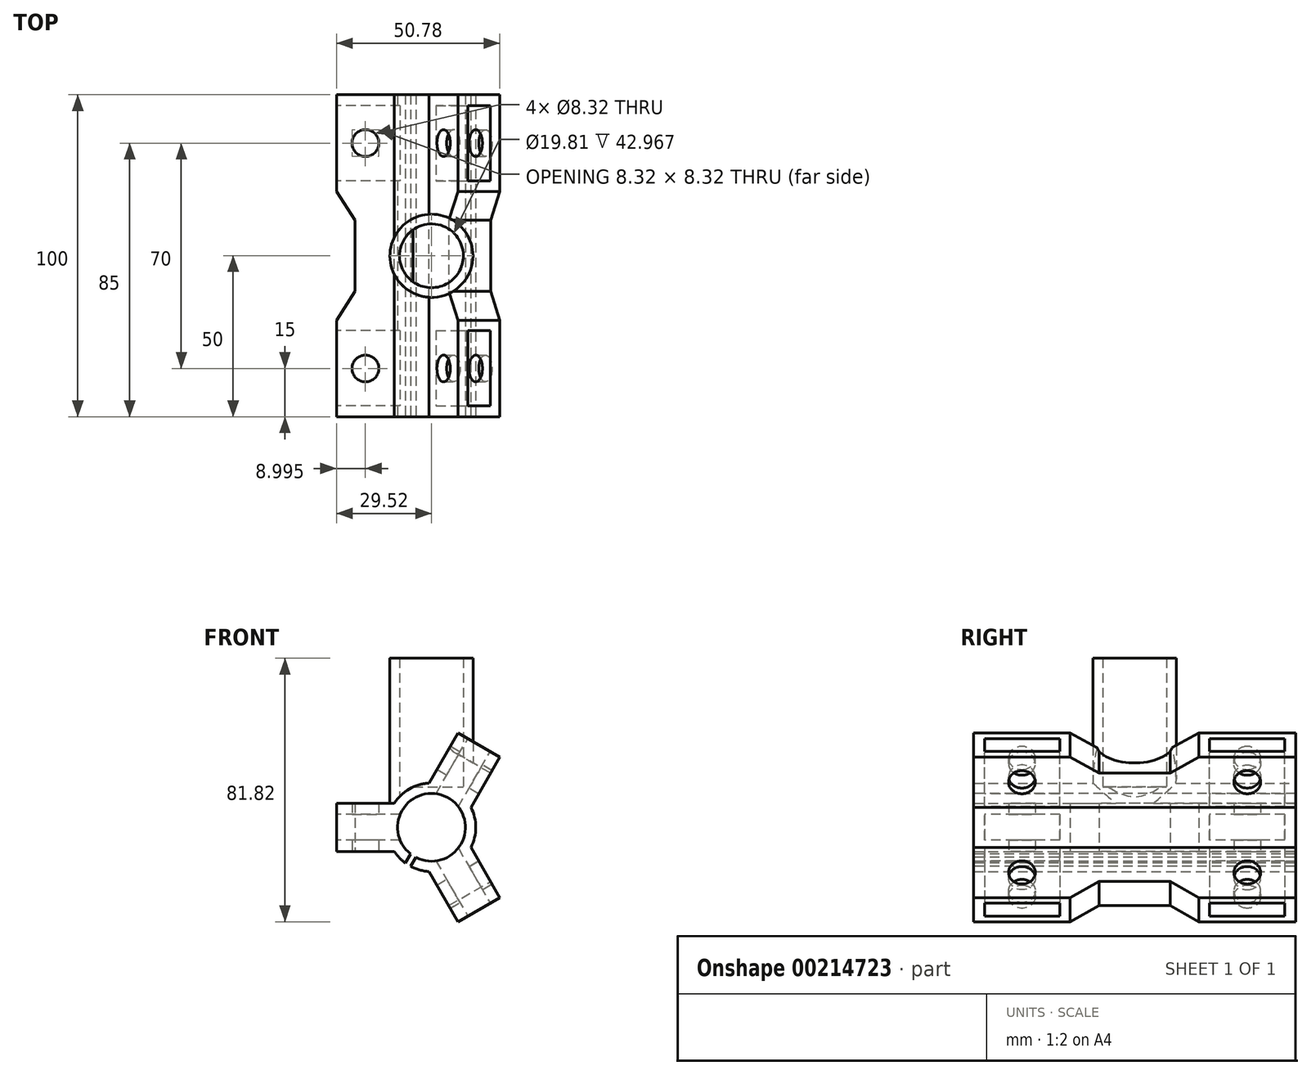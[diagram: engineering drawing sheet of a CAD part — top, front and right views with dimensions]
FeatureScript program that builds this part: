
annotation { "Feature Type Name" : "Feature", "Feature Type Description" : "" }
export const myFeature = defineFeature(function(context is Context, id is Id, definition is map)
    precondition{}
    {
        {
            var Q0;
            Q0=qCreatedBy(makeId("Top.planeOp"),FACE);
            var sketch = newSketch(context, id + "F0", { "sketchPlane" : qUnion([Q0])});
            skLineSegment(sketch, "E0", {"start": v(0, 0) * mm, "end": v(-9.53, 0) * mm, "construction": true});
            skLineSegment(sketch, "E1", {"start": v(-9.53, 0) * mm, "end": v(-9.53, 50) * mm, "construction": true});
            skLineSegment(sketch, "E2", {"start": v(-11.52, 0) * mm, "end": v(-11.53, 50) * mm});
            skLineSegment(sketch, "E3", {"start": v(-11.52, 0) * mm, "end": v(-29.52, 0) * mm});
            skLineSegment(sketch, "E4", {"start": v(-29.52, 0) * mm, "end": v(-29.53, 30) * mm});
            skCircle(sketch, "E5", {"center": v(-20.53, 15) * mm, "radius": 11 * mm, "construction": true});
            skCircle(sketch, "E6", {"center": v(-20.53, 15) * mm, "radius": 4.16 * mm});
            skLineSegment(sketch, "E7", {"start": v(-11.53, 39) * mm, "end": v(-23.75, 39) * mm, "construction": true});
            skLineSegment(sketch, "E8", {"start": v(-29.53, 30) * mm, "end": v(-23.75, 39) * mm});
            skLineSegment(sketch, "E9", {"start": v(-23.75, 39) * mm, "end": v(-23.75, 50) * mm});
            skLineSegment(sketch, "E10", {"start": v(-11.53, 50) * mm, "end": v(-23.75, 50) * mm, "construction": true});
            skLineSegment(sketch, "E11.MirrorCS", {"start": v(-23.75, 61) * mm, "end": v(-23.75, 50) * mm});
            skLineSegment(sketch, "E12.MirrorCS", {"start": v(-29.52, 70) * mm, "end": v(-23.75, 61) * mm});
            skLineSegment(sketch, "E13.MirrorCS", {"start": v(-29.53, 100) * mm, "end": v(-29.53, 70) * mm});
            skLineSegment(sketch, "E14.MirrorCS", {"start": v(-11.52, 100) * mm, "end": v(-29.52, 100) * mm});
            skLineSegment(sketch, "E15.MirrorCS", {"start": v(-11.53, 100) * mm, "end": v(-11.53, 50) * mm});
            skCircle(sketch, "E16.MirrorC", {"center": v(-20.53, 85) * mm, "radius": 4.16 * mm});
            skLineSegment(sketch, "E17.MirrorCS", {"start": v(-9.53, 100) * mm, "end": v(-9.53, 50) * mm, "construction": true});
            skCircle(sketch, "E18.MirrorC", {"center": v(-20.53, 85) * mm, "radius": 11 * mm, "construction": true});
            skSolve(sketch);
        }
        {
            var Q0;
            Q0=makeQuery(id+"F0.imprint","IMPRINT",FACE,{"disambiguationData":[TD([[makeQuery(id+"F0.imprint","IMPRINT",EDGE,{"derivedFrom":sQuery(id+"F0.wireOp",EDGE,"E2")}),1.0]])]});
            extrude(context, id + "F1", {"entities" : qUnion([Q0]), "depth" : 15 * mm});
        }
        {
            var Q0;
            Q0=makeQuery(id+"F1.opExtrude","SWEPT_FACE",FACE,{"disambiguationData":[OSD([sQuery(id+"F0.wireOp",EDGE,"E3")])]});
            var sketch = newSketch(context, id + "F2", { "sketchPlane" : qUnion([Q0])});
            skCircle(sketch, "E19", {"center": v(0, 7.5) * mm, "radius": 13.75 * mm, "construction": true});
            skCircle(sketch, "E20", {"center": v(0, 7.5) * mm, "radius": 10.53 * mm, "construction": true});
            skPoint(sketch, "E21.endSnap0", {"position": v(-11.52, 7.5) * mm});
            skArc(sketch, "E22", {"start": v(-6.88, 19.4) * mm, "mid": v(-13.75, 7.5) * mm, "end": v(-6.88, -4.4) * mm});
            skLineSegment(sketch, "E23", {"start": v(0, 7.5) * mm, "end": v(-10.53, 7.5) * mm, "construction": true});
            skLineSegment(sketch, "E24", {"start": v(0, 7.5) * mm, "end": v(-5.26, -1.61) * mm, "construction": true});
            skLineSegment(sketch, "E25", {"start": v(0, 7.5) * mm, "end": v(-5.26, 16.61) * mm, "construction": true});
            skArc(sketch, "E26", {"start": v(-5.26, 16.61) * mm, "mid": v(-10.53, 7.5) * mm, "end": v(-5.26, -1.61) * mm});
            skLineSegment(sketch, "E27", {"start": v(-5.26, 16.61) * mm, "end": v(-6.88, 19.4) * mm});
            skLineSegment(sketch, "E28", {"start": v(-5.26, -1.61) * mm, "end": v(-6.88, -4.4) * mm});
            skCircle(sketch, "E29", {"center": v(0, 7.5) * mm, "radius": 9.53 * mm, "construction": true});
            skSolve(sketch);
        }
        {
            var Q0;
            {var subQ0=sQuery(id+"F2.wireOp",EDGE,"E19");var subQ1=sQuery(id+"F0.wireOp",EDGE,"E3");var subQ2=makeQuery(id+"F1.opExtrude","SWEPT_EDGE",EDGE,{"disambiguationData":[OSD([sQuery(id+"F0.wireOp",EDGE,"E2"),subQ1])]});var subQ3=makeQuery(id+"F2.imprint","INTERSECT",VERTEX,{"derivedFrom":[subQ2,makeQuery(id+"F1.opExtrude","CAP_EDGE",EDGE,{"disambiguationData":[OSD([subQ1])],"isStart":true}),subQ0]});Q0=makeQuery(id+"F2.imprint","IMPRINT",FACE,{"disambiguationData":[TD([[makeQuery(id+"F2.imprint","IMPRINT",EDGE,{"disambiguationData":[TD([[subQ3,1.0]])],"derivedFrom":subQ0}),1.0]])]});}
            var Q1;
            {var subQ0=sQuery(id+"F2.wireOp",EDGE,"g3xJxAlq-R5pZ-Eeo2-CjEf-WmfwMOpCXLWw");Q1=makeQuery(id+"F2.imprint","IMPRINT",FACE,{"disambiguationData":[TD([[makeQuery(id+"F2.imprint","IMPRINT",EDGE,{"derivedFrom":subQ0}),-1.0]])]});}
            var Q2;
            Q2=makeQuery(id+"F2.imprint","IMPRINT",FACE,{"disambiguationData":[TD([[makeQuery(id+"F2.imprint","IMPRINT",EDGE,{"derivedFrom":sQuery(id+"F2.wireOp",EDGE,"E20")}),-1.0]])]});
            var Q3;
            Q3=makeQuery(id+"F2.imprint","IMPRINT",FACE,{"disambiguationData":[TD([[makeQuery(id+"F2.imprint","IMPRINT",EDGE,{"derivedFrom":sQuery(id+"F2.wireOp",EDGE,"E26")}),-1.0]])]});
            extrude(context, id + "F3", {"entities" : qUnion([Q0, Q1, Q2, Q3]), "operationType" : NewBodyOperationType.ADD, "oppositeDirection" : true, "depth" : 100 * mm});
        }
        {
            var Q0;
            Q0=makeQuery(id+"F1.opExtrude","SWEPT_FACE",FACE,{"disambiguationData":[OSD([sQuery(id+"F0.wireOp",EDGE,"E13.MirrorCS")])]});
            var sketch = newSketch(context, id + "F4", { "sketchPlane" : qUnion([Q0])});
            skLineSegment(sketch, "E30.bottom", {"start": v(-96.6, 11.5) * mm, "end": v(-73.2, 11.5) * mm});
            skLineSegment(sketch, "E30.top", {"start": v(-96.6, 3.5) * mm, "end": v(-73.2, 3.5) * mm});
            skLineSegment(sketch, "E30.left", {"start": v(-96.6, 11.5) * mm, "end": v(-96.6, 3.5) * mm});
            skLineSegment(sketch, "E30.right", {"start": v(-73.2, 11.5) * mm, "end": v(-73.2, 3.5) * mm});
            skLineSegment(sketch, "E31.bottom", {"start": v(-3.4, 3.5) * mm, "end": v(-26.8, 3.5) * mm});
            skLineSegment(sketch, "E31.top", {"start": v(-3.4, 11.5) * mm, "end": v(-26.8, 11.5) * mm});
            skLineSegment(sketch, "E31.left", {"start": v(-3.4, 3.5) * mm, "end": v(-3.4, 11.5) * mm});
            skLineSegment(sketch, "E31.right", {"start": v(-26.8, 3.5) * mm, "end": v(-26.8, 11.5) * mm});
            skSolve(sketch);
        }
        {
            var Q0;
            Q0=makeQuery(id+"F4.imprint","IMPRINT",FACE,{"disambiguationData":[TD([[makeQuery(id+"F4.imprint","IMPRINT",EDGE,{"derivedFrom":sQuery(id+"F4.wireOp",EDGE,"E30.bottom")}),-1.0]])]});
            var Q1;
            Q1=makeQuery(id+"F4.imprint","IMPRINT",FACE,{"disambiguationData":[TD([[makeQuery(id+"F4.imprint","IMPRINT",EDGE,{"derivedFrom":sQuery(id+"F4.wireOp",EDGE,"E31.bottom")}),-1.0]])]});
            extrude(context, id + "F5", {"entities" : qUnion([Q0, Q1]), "operationType" : NewBodyOperationType.REMOVE, "oppositeDirection" : true, "depth" : 25 * mm});
        }
        {
            var Q0;
            {var subQ0=sQuery(id+"F0.wireOp",EDGE,"E3");Q0=makeQuery(id+"F3.boolean.opBoolean","MERGE",FACE,{"derivedFrom":[makeQuery(id+"F1.opExtrude","SWEPT_FACE",FACE,{"disambiguationData":[OSD([subQ0])]}),makeQuery(id+"F3.opExtrude","CAP_FACE",FACE,{"disambiguationData":[OSD([sQuery(id+"F0.wireOp",EDGE,"E2"),subQ0,sQuery(id+"F2.wireOp",EDGE,"E22"),sQuery(id+"F2.wireOp",EDGE,"E26"),sQuery(id+"F2.wireOp",EDGE,"E27"),sQuery(id+"F2.wireOp",EDGE,"E28")])],"isStart":true})]});}
            var sketch = newSketch(context, id + "F6", { "sketchPlane" : qUnion([Q0])});
            skCircle(sketch, "E32", {"center": v(0, 7.5) * mm, "radius": 10.53 * mm});
            skSolve(sketch);
        }
        {
            var Q0;
            Q0=makeQuery(id+"F1.opExtrude","SWEPT_BODY",BODY,{"disambiguationData":[OSD([sQuery(id+"F0.wireOp",EDGE,"E2"),sQuery(id+"F0.wireOp",EDGE,"E3"),sQuery(id+"F0.wireOp",EDGE,"E4"),sQuery(id+"F0.wireOp",EDGE,"E6"),sQuery(id+"F0.wireOp",EDGE,"E8"),sQuery(id+"F0.wireOp",EDGE,"E9"),sQuery(id+"F0.wireOp",EDGE,"E11.MirrorCS"),sQuery(id+"F0.wireOp",EDGE,"E12.MirrorCS"),sQuery(id+"F0.wireOp",EDGE,"E13.MirrorCS"),sQuery(id+"F0.wireOp",EDGE,"E14.MirrorCS"),sQuery(id+"F0.wireOp",EDGE,"E15.MirrorCS"),sQuery(id+"F0.wireOp",EDGE,"E16.MirrorC")])]});
            var Q1;
            Q1=sQuery(id+"F6.wireOp",EDGE,"E32");
            circularPattern(context, id + "F7", {"operationType" : NewBodyOperationType.ADD, "entities" : qUnion([Q0]), "axis" : qUnion([Q1]), "angle" : 360 * degree, "instanceCount" : 3, "equalSpace" : true, "computeTransformsWithoutBuiltin" : true});
        }
        {
            var Q0;
            Q0=qCreatedBy(makeId("Top.planeOp"),FACE);
            var sketch = newSketch(context, id + "F8", { "sketchPlane" : qUnion([Q0])});
            skCircle(sketch, "E33", {"center": v(0, 50) * mm, "radius": 9.9 * mm});
            skCircle(sketch, "E34", {"center": v(0, 50) * mm, "radius": 12.9 * mm});
            skSolve(sketch);
        }
        {
            var Q0;
            Q0=makeQuery(id+"F8.imprint","IMPRINT",FACE,{"disambiguationData":[TD([[makeQuery(id+"F8.imprint","IMPRINT",EDGE,{"derivedFrom":sQuery(id+"F8.wireOp",EDGE,"E33")}),-1.0]])]});
            extrude(context, id + "F9", {"entities" : qUnion([Q0]), "operationType" : NewBodyOperationType.ADD, "depth" : 60 * mm, "hasSecondDirection" : true, "secondDirectionOppositeDirection" : false, "secondDirectionDepth" : 15 * mm});
        }
        {
            var Q0;
            Q0=makeQuery(id+"F9.opExtrude","CAP_FACE",FACE,{"disambiguationData":[OSD([sQuery(id+"F8.wireOp",EDGE,"E33"),sQuery(id+"F8.wireOp",EDGE,"E34")])],"isStart":false});
            var sketch = newSketch(context, id + "F10", { "sketchPlane" : qUnion([Q0])});
            skCircle(sketch, "E35", {"center": v(0, 50) * mm, "radius": 9.9 * mm});
            skSolve(sketch);
        }
        {
            var Q0;
            Q0=makeQuery(id+"F10.imprint","IMPRINT",FACE,{"disambiguationData":[TD([[makeQuery(id+"F10.imprint","IMPRINT",EDGE,{"derivedFrom":sQuery(id+"F10.wireOp",EDGE,"E35")}),1.0]])]});
            extrude(context, id + "F11", {"entities" : qUnion([Q0]), "operationType" : NewBodyOperationType.REMOVE, "oppositeDirection" : true, "depth" : 40 * mm});
        }
        {
            var Q0;
            {var subQ0=sQuery(id+"F0.wireOp",EDGE,"E3");var subQ1=makeQuery(id+"F3.boolean.opBoolean","MERGE",FACE,{"derivedFrom":[makeQuery(id+"F1.opExtrude","SWEPT_FACE",FACE,{"disambiguationData":[OSD([subQ0])]}),makeQuery(id+"F3.opExtrude","CAP_FACE",FACE,{"disambiguationData":[OSD([sQuery(id+"F0.wireOp",EDGE,"E2"),subQ0,sQuery(id+"F2.wireOp",EDGE,"E22"),sQuery(id+"F2.wireOp",EDGE,"E26"),sQuery(id+"F2.wireOp",EDGE,"E27"),sQuery(id+"F2.wireOp",EDGE,"E28")])],"isStart":true})]});Q0=makeQuery(id+"F7.boolean.opBoolean","MERGE",FACE,{"derivedFrom":[subQ1,makeQuery(id+"F7.opPattern","COPY",FACE,{"derivedFrom":subQ1,"instanceName":"1"}),makeQuery(id+"F7.opPattern","COPY",FACE,{"derivedFrom":subQ1,"instanceName":"2"})]});}
            var sketch = newSketch(context, id + "F12", { "sketchPlane" : qUnion([Q0])});
            skLineSegment(sketch, "E36", {"start": v(-1.17, -5.98) * mm, "end": v(-11.96, 0.25) * mm, "construction": true});
            skLineSegment(sketch, "E37", {"start": v(-6.56, -2.87) * mm, "end": v(-8.22, -5.74) * mm, "construction": true});
            skLineSegment(sketch, "E38", {"start": v(-8.22, -5.74) * mm, "end": v(-7.36, -6.24) * mm});
            skLineSegment(sketch, "E39", {"start": v(-8.22, -5.74) * mm, "end": v(-9.09, -5.24) * mm});
            skLineSegment(sketch, "E40", {"start": v(-9.09, -5.24) * mm, "end": v(-6.5, -0.77) * mm});
            skLineSegment(sketch, "E41", {"start": v(-7.36, -6.24) * mm, "end": v(-4.78, -1.77) * mm});
            skLineSegment(sketch, "E42", {"start": v(-6.5, -0.77) * mm, "end": v(-4.78, -1.77) * mm});
            skSolve(sketch);
        }
        {
            var Q0;
            {var subQ0=sQuery(id+"F12.wireOp",EDGE,"E42");var subQ1=sQuery(id+"F12.wireOp",EDGE,"E40");var subQ2=makeQuery(id+"F3.opExtrude","CAP_EDGE",EDGE,{"disambiguationData":[OSD([sQuery(id+"F2.wireOp",EDGE,"E26")])],"isStart":true});var subQ3=makeQuery(id+"F7.boolean.opBoolean","MERGE",EDGE,{"derivedFrom":[subQ2,makeQuery(id+"F7.opPattern","COPY",EDGE,{"derivedFrom":subQ2,"instanceName":"1"}),makeQuery(id+"F7.opPattern","COPY",EDGE,{"derivedFrom":subQ2,"instanceName":"2"})]});var subQ4=makeQuery(id+"F12.imprint","INTERSECT",VERTEX,{"derivedFrom":[subQ3,subQ1,subQ0]});Q0=makeQuery(id+"F12.imprint","IMPRINT",FACE,{"disambiguationData":[TD([[makeQuery(id+"F12.imprint","IMPRINT",EDGE,{"disambiguationData":[TD([[subQ4,1.0]])],"derivedFrom":subQ1}),-1.0]])]});}
            extrude(context, id + "F13", {"entities" : qUnion([Q0]), "operationType" : NewBodyOperationType.REMOVE, "oppositeDirection" : true, "depth" : 130 * mm});
        }
        {
            var Q0;
            {var subQ0=sQuery(id+"F0.wireOp",EDGE,"E3");var subQ1=makeQuery(id+"F3.boolean.opBoolean","MERGE",FACE,{"derivedFrom":[makeQuery(id+"F1.opExtrude","SWEPT_FACE",FACE,{"disambiguationData":[OSD([subQ0])]}),makeQuery(id+"F3.opExtrude","CAP_FACE",FACE,{"disambiguationData":[OSD([sQuery(id+"F0.wireOp",EDGE,"E2"),subQ0,sQuery(id+"F2.wireOp",EDGE,"E22"),sQuery(id+"F2.wireOp",EDGE,"E26"),sQuery(id+"F2.wireOp",EDGE,"E27"),sQuery(id+"F2.wireOp",EDGE,"E28")])],"isStart":true})]});Q0=makeQuery(id+"F7.boolean.opBoolean","MERGE",FACE,{"derivedFrom":[subQ1,makeQuery(id+"F7.opPattern","COPY",FACE,{"derivedFrom":subQ1,"instanceName":"1"}),makeQuery(id+"F7.opPattern","COPY",FACE,{"derivedFrom":subQ1,"instanceName":"2"})]});}
            var sketch = newSketch(context, id + "F14", { "sketchPlane" : qUnion([Q0])});
            skCircle(sketch, "E43", {"center": v(0, 7.5) * mm, "radius": 10.53 * mm});
            skSolve(sketch);
        }
        {
            var Q0;
            {var subQ0=sQuery(id+"F14.wireOp",EDGE,"E43");var subQ1=makeQuery(id+"F14.imprint","INTERSECT",VERTEX,{"derivedFrom":[makeQuery(id+"F13.boolean.opBoolean","COPY",EDGE,{"derivedFrom":makeQuery(id+"F13.opExtrude","CAP_EDGE",EDGE,{"disambiguationData":[OSD([sQuery(id+"F12.wireOp",EDGE,"E40")])],"isStart":true})}),subQ0]});Q0=makeQuery(id+"F14.imprint","IMPRINT",FACE,{"disambiguationData":[TD([[makeQuery(id+"F14.imprint","IMPRINT",EDGE,{"disambiguationData":[TD([[subQ1,1.0]])],"derivedFrom":subQ0}),1.0]])]});}
            extrude(context, id + "F15", {"entities" : qUnion([Q0]), "operationType" : NewBodyOperationType.REMOVE, "oppositeDirection" : true, "depth" : 100 * mm});
        }
    });
